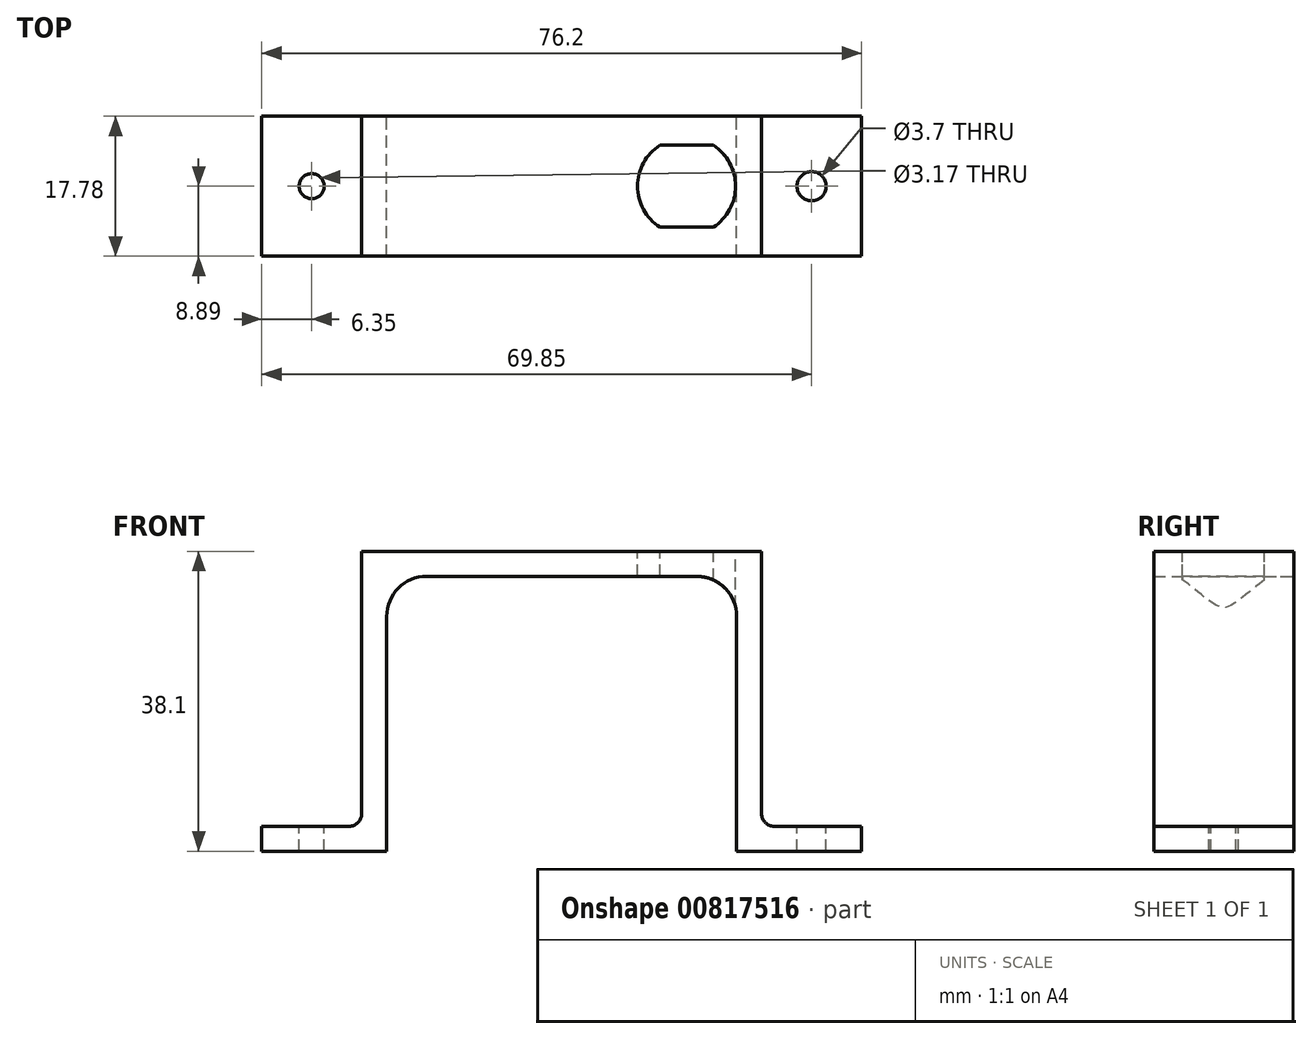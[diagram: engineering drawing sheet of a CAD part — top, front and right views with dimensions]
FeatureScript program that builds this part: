
annotation { "Feature Type Name" : "Feature", "Feature Type Description" : "" }
export const myFeature = defineFeature(function(context is Context, id is Id, definition is map)
    precondition{}
    {
        {
            var Q0;
            Q0=qCreatedBy(makeId("Front.planeOp"),FACE);
            var sketch = newSketch(context, id + "F0", { "sketchPlane" : qUnion([Q0])});
            skLineSegment(sketch, "E0", {"start": v(-38.1, 0) * mm, "end": v(-22.23, 0) * mm});
            skLineSegment(sketch, "E1", {"start": v(-22.23, 0) * mm, "end": v(-22.23, 34.92) * mm});
            skLineSegment(sketch, "E2", {"start": v(-22.23, 34.92) * mm, "end": v(22.23, 34.92) * mm});
            skLineSegment(sketch, "E3", {"start": v(22.22, 34.92) * mm, "end": v(22.23, 0) * mm});
            skLineSegment(sketch, "E4", {"start": v(22.23, 0) * mm, "end": v(38.1, 0) * mm});
            skLineSegment(sketch, "E5.0", {"start": v(25.4, 3.17) * mm, "end": v(38.1, 3.17) * mm});
            skLineSegment(sketch, "E5.1", {"start": v(-38.1, 3.17) * mm, "end": v(-25.4, 3.17) * mm});
            skLineSegment(sketch, "E5.2", {"start": v(-25.4, 3.18) * mm, "end": v(-25.4, 38.1) * mm});
            skLineSegment(sketch, "E5.3", {"start": v(-25.4, 38.1) * mm, "end": v(25.4, 38.1) * mm});
            skLineSegment(sketch, "E5.4", {"start": v(25.4, 38.1) * mm, "end": v(25.4, 3.18) * mm});
            skLineSegment(sketch, "E6", {"start": v(-38.1, 3.17) * mm, "end": v(-38.1, 0) * mm});
            skLineSegment(sketch, "E7", {"start": v(38.1, 3.17) * mm, "end": v(38.1, 0) * mm});
            skSolve(sketch);
        }
        {
            var Q0;
            Q0 = qSketchRegion(id + "F0", true);
            extrude(context, id + "F1", {"entities" : qUnion([Q0]), "endBound" : BoundingType.SYMMETRIC, "depth" : 17.78 * mm, "offsetDistance" : 25.4 * mm});
        }
        {
            var Q0;
            Q0=makeQuery(id+"F1.opExtrude","SWEPT_FACE",FACE,{"disambiguationData":[OSD([sQuery(id+"F0.wireOp",EDGE,"E5.0")])]});
            var sketch = newSketch(context, id + "F2", { "sketchPlane" : qUnion([Q0])});
            skCircle(sketch, "E8", {"center": v(-31.75, 0) * mm, "radius": 1.59 * mm});
            skCircle(sketch, "E9", {"center": v(31.75, 0) * mm, "radius": 1.85 * mm});
            skSolve(sketch);
        }
        {
            var Q0;
            Q0 = qSketchRegion(id + "F2", true);
            extrude(context, id + "F3", {"entities" : qUnion([Q0]), "operationType" : NewBodyOperationType.REMOVE, "endBound" : BoundingType.THROUGH_ALL, "oppositeDirection" : true, "depth" : 25.4 * mm, "offsetDistance" : 25.4 * mm});
        }
        {
            var Q0;
            Q0=makeQuery(id+"F1.opExtrude","SWEPT_FACE",FACE,{"disambiguationData":[OSD([sQuery(id+"F0.wireOp",EDGE,"E5.3")])]});
            var sketch = newSketch(context, id + "F4", { "sketchPlane" : qUnion([Q0])});
            skArc(sketch, "E10", {"start": v(12.47, 5.2) * mm, "mid": v(9.65, 0) * mm, "end": v(12.47, -5.2) * mm});
            skLineSegment(sketch, "E11", {"start": v(12.47, 5.2) * mm, "end": v(19.28, 5.2) * mm});
            skLineSegment(sketch, "E12", {"start": v(19.28, -5.2) * mm, "end": v(12.47, -5.2) * mm});
            skArc(sketch, "E13.trimOffspring", {"start": v(19.28, -5.2) * mm, "mid": v(22.1, 0) * mm, "end": v(19.28, 5.2) * mm});
            skSolve(sketch);
        }
        {
            var Q0;
            Q0 = qSketchRegion(id + "F4", true);
            extrude(context, id + "F5", {"entities" : qUnion([Q0]), "operationType" : NewBodyOperationType.REMOVE, "endBound" : BoundingType.THROUGH_ALL, "oppositeDirection" : true, "depth" : 25.4 * mm, "offsetDistance" : 25.4 * mm});
        }
        {
            var Q0;
            Q0=makeQuery(id+"F1.opExtrude","SWEPT_EDGE",EDGE,{"disambiguationData":[OSD([sQuery(id+"F0.wireOp",EDGE,"E1"),sQuery(id+"F0.wireOp",EDGE,"E2")])]});
            var Q1;
            Q1=makeQuery(id+"F1.opExtrude","SWEPT_EDGE",EDGE,{"disambiguationData":[OSD([sQuery(id+"F0.wireOp",EDGE,"E2"),sQuery(id+"F0.wireOp",EDGE,"E3")])]});
            fillet(context, id + "F6", {"entities" : qUnion([Q0, Q1]), "radius" : 5.08 * mm, "tangentPropagation" : true, "allowEdgeOverflow" : false});
        }
        {
            var Q0;
            Q0=makeQuery(id+"F1.opExtrude","SWEPT_EDGE",EDGE,{"disambiguationData":[OSD([sQuery(id+"F0.wireOp",EDGE,"E5.1"),sQuery(id+"F0.wireOp",EDGE,"E5.2")])]});
            var Q1;
            Q1=makeQuery(id+"F1.opExtrude","SWEPT_EDGE",EDGE,{"disambiguationData":[OSD([sQuery(id+"F0.wireOp",EDGE,"E5.0"),sQuery(id+"F0.wireOp",EDGE,"E5.4")])]});
            fillet(context, id + "F7", {"entities" : qUnion([Q0, Q1]), "radius" : 1.6 * mm, "tangentPropagation" : true, "allowEdgeOverflow" : false});
        }
    });
